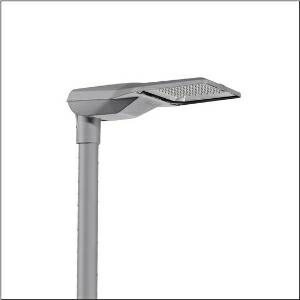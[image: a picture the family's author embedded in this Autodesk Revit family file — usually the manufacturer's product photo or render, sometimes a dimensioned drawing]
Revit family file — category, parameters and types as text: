
# Revit family: streetlight_sl_21_iq_midi___pc-l_5xe3f31g08mb_a45c
name_source: partatom
category: Lighting Fixtures
units: mm (PartAtom-declared; Revit-internal decimal feet)

## family parameters
Cut with Voids When Loaded = No
Host = Face
Light Source = No
Part Type = Normal
Room Calculation Point = No
Round Connector Dimension = Use Diameter
Shared = No

## types (1)
- --- (1 x LED, 18560 lm, 146.7 W, 3000K)
    Apparent Load = 147 VA
    CIE Flux Codes = 38 78 98 100 100
    Color Rendering = 70
    Color Temperature = 3000K
    Default Elevation = 1800 mm
    Description = Streetlight SL 21 iQ midi, mast luminaire, primary light control with lens, of PMMA, primary optical cover: cover, of toughened safety glass, transparent, light distribution: PC-L, light emission: direct distribution, primary light characteristic: asymmetric, left, installation type: post-top, side-entry, LED, High Power LED, rated luminous flux: 18.560lm, luminous efficacy: 127lm/W, light colour: 730, colour temperature: 3000K, control gear: iQ Street-Remote, control: Street-Remote, Auto-Match, Temp-Guard, Lumen-Switch, Night-Set, Smart-Wire, Light-Fading, Desk-Remote (wireless, voltage-free reading and setting of iQ features in the workshop via application-optimized NFC function/RFID function), optimised constant luminous flux control (CLO 2.0), pre-setting: linear dimming characteristic, mains connection: 230..240V, AC, 50/60Hz, start of lifetime: 147W, end of service life: 161W, reduction: 62W, luminaire housing, of diecast aluminium, powder-coated, SITECO metallic grey (DB 702S), corrosivity category C5 high according to DIN EN ISO 12944, please order mast flange separately, inclination adjustable: 0°, 5°, 10°, 15°, sealing non-destructively replaceable, multi-level sealing system, length: 644mm, width: 335mm, height: 110mm, mast flange for spigot size: 42mm (side-entry): 5XC10008XM4, 60/48mm (side-entry/post-top): 5XC10108XM2, 76/60mm (side-entry/post-top): 5XC10108XM1, mounting height: 4..8m, protection rating (complete): IP66, insulation class (complete): insulation class II (safety insulation), certification: CE, ENEC, ENEC+, VDE, impact resistance: IK10, permissible operating ambient temperature for outdoor applications: -40..+50°C, standard-compliant lighting for roads and squares, packaging unit: 1 piece

Light Distribution: PC-L
    Height = 111 mm
    Lamp = 1 x LED
    Lamp Light Flux = 18560 lm
    Lamp Power = 146.7 W
    Lamp count = 1
    Length = 644 mm
    Luminous efficacy = 127 lm/W
    Manufacturer = Siteco
    ModVariant = No
    Model = 5XE3F31G08MB
    Number of Poles = 1
    OnlyDefault = Yes
    Power Factor = 1
    Product Name = Streetlight SL 21 iQ midi | PC-L
    Product group = mast luminaire | pylon top
    ProductGroupID = 6100
    Protection Class = Protection class II
    Protection Degree = IP 66
    RLX_Detail_Level = 1
    RLX_Emergency_Light_Flux = 0 lm
    RLX_Emergency_Type = 0
    RLX_Emergency_Type_DB = No
    RlxData = <blob elided: 29465 chars, md5=4ff337d3>
    Socket = socket
    Standby Power = 0 W
    System Light Flux = 18560 lm
    System Power = 147 W
    Type Comments = factory setting: luminous flux: 100 % | dim-lin: 254 | 753 mA
    Type Image = l_1004298.jpg
    URL = http://relux.com
    VarID = @adj_072079
    Voltage = 0 V
    Weight = 0.00 kg
    Width = 336 mm

## geometry (parser evidence)
native form markers: Blend x4, Sweep x10
no freeform markers — native parametric forms only
